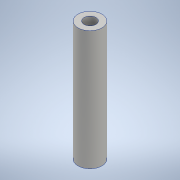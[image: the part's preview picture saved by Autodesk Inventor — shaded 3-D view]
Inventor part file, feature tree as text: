
AUTODESK INVENTOR PART (.ipt)
format: ipt  version: 2020.2 (Build 242310000, 310)  size: 114,176 bytes
history: native  units: mm
features: sketch x2, extrude x2, hole x2, other x1
ambient origin geometry x8: Origin, YZ Plane, XZ Plane, XY Plane, X Axis, Y Axis, Z Axis, Center Point
bodies: Body1 (feature_tree)
feature tree (7):
  other  "ソリッド1"
  sketch  "スケッチ1"
  extrude  "押し出し1"  Depth=6.0mm
  sketch  "スケッチ2"
  extrude  "押し出し2"  Depth=3.001mm
  hole  "穴1"  [1 undecoded]
  hole  "穴2"  [1 undecoded]
note: 2 required parameter values undecoded (feature->parameter linkage not recoverable at this tier; creation-order binding heuristic only, values carry confidence <= 0.55)
